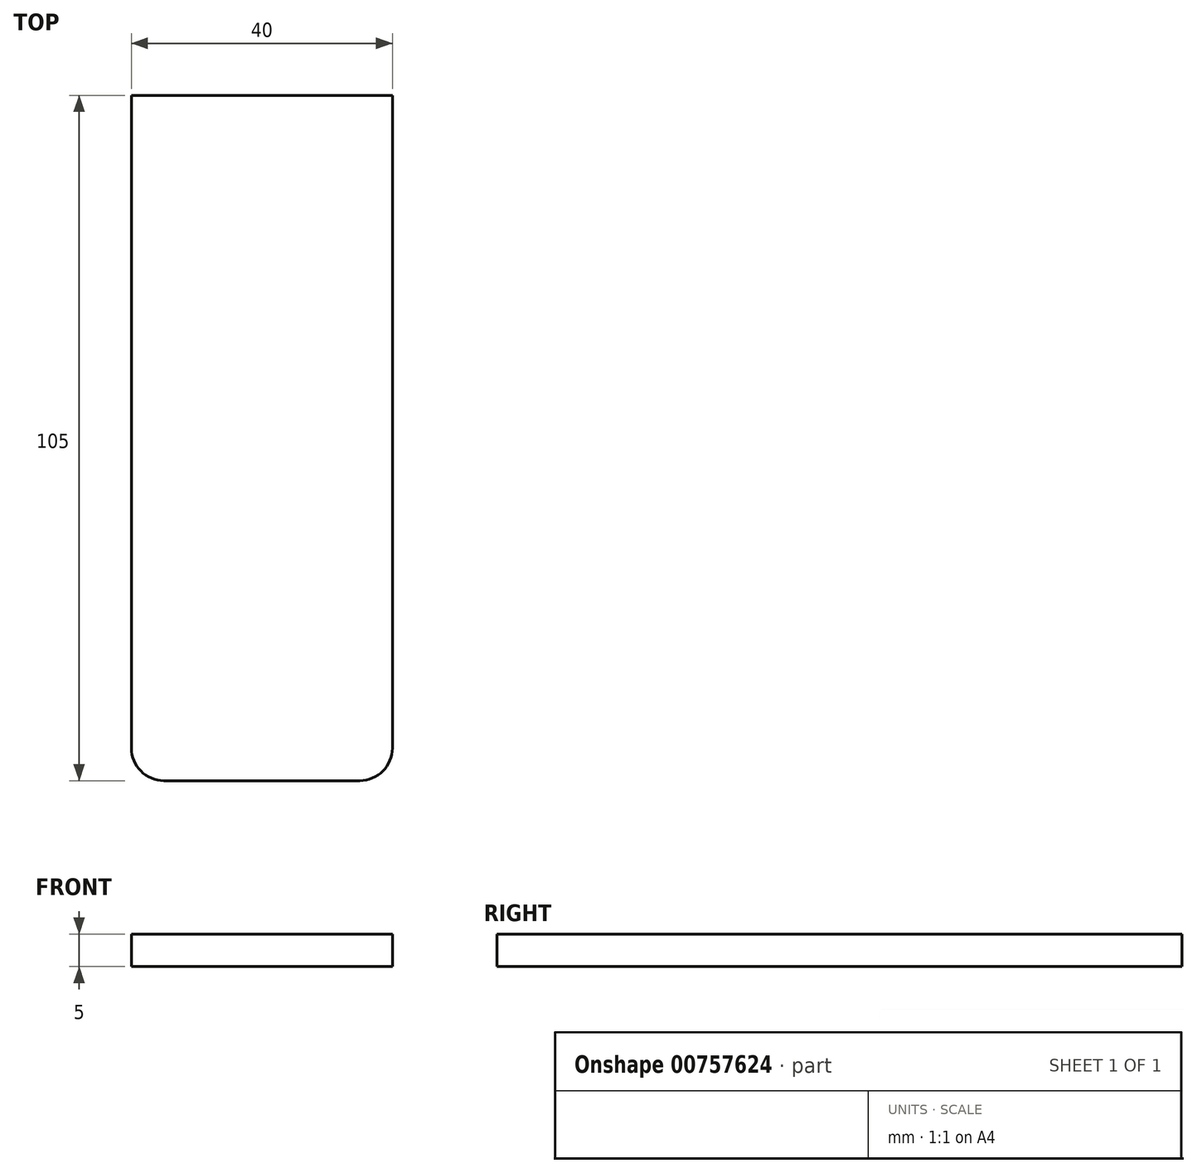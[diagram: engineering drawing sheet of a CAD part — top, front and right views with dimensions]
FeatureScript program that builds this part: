
annotation { "Feature Type Name" : "Feature", "Feature Type Description" : "" }
export const myFeature = defineFeature(function(context is Context, id is Id, definition is map)
    precondition{}
    {
        {
            var Q0;
            Q0=qCreatedBy(makeId("Top.planeOp"),FACE);
            var sketch = newSketch(context, id + "F0", { "sketchPlane" : qUnion([Q0])});
            skLineSegment(sketch, "E0.bottom", {"start": v(-20, 50) * mm, "end": v(20, 50) * mm});
            skLineSegment(sketch, "E0.top", {"start": v(-15, -55) * mm, "end": v(15, -55) * mm});
            skLineSegment(sketch, "E0.left", {"start": v(-20, 50) * mm, "end": v(-20, -50) * mm});
            skLineSegment(sketch, "E0.right", {"start": v(20, 50) * mm, "end": v(20, -50) * mm});
            skPoint(sketch, "E1.visualSharp", {"position": v(-20, -55) * mm});
            skArc(sketch, "E1.filletArc", {"start": v(-20, -50) * mm, "mid": v(-18.54, -53.54) * mm, "end": v(-15, -55) * mm});
            skPoint(sketch, "E2.visualSharp", {"position": v(20, -55) * mm});
            skArc(sketch, "E2.filletArc", {"start": v(15, -55) * mm, "mid": v(18.54, -53.54) * mm, "end": v(20, -50) * mm});
            skSolve(sketch);
        }
        {
            var Q0;
            Q0 = qSketchRegion(id + "F0", true);
            extrude(context, id + "F1", {"entities" : qUnion([Q0]), "depth" : 5 * mm, "offsetDistance" : 25 * mm});
        }
    });
